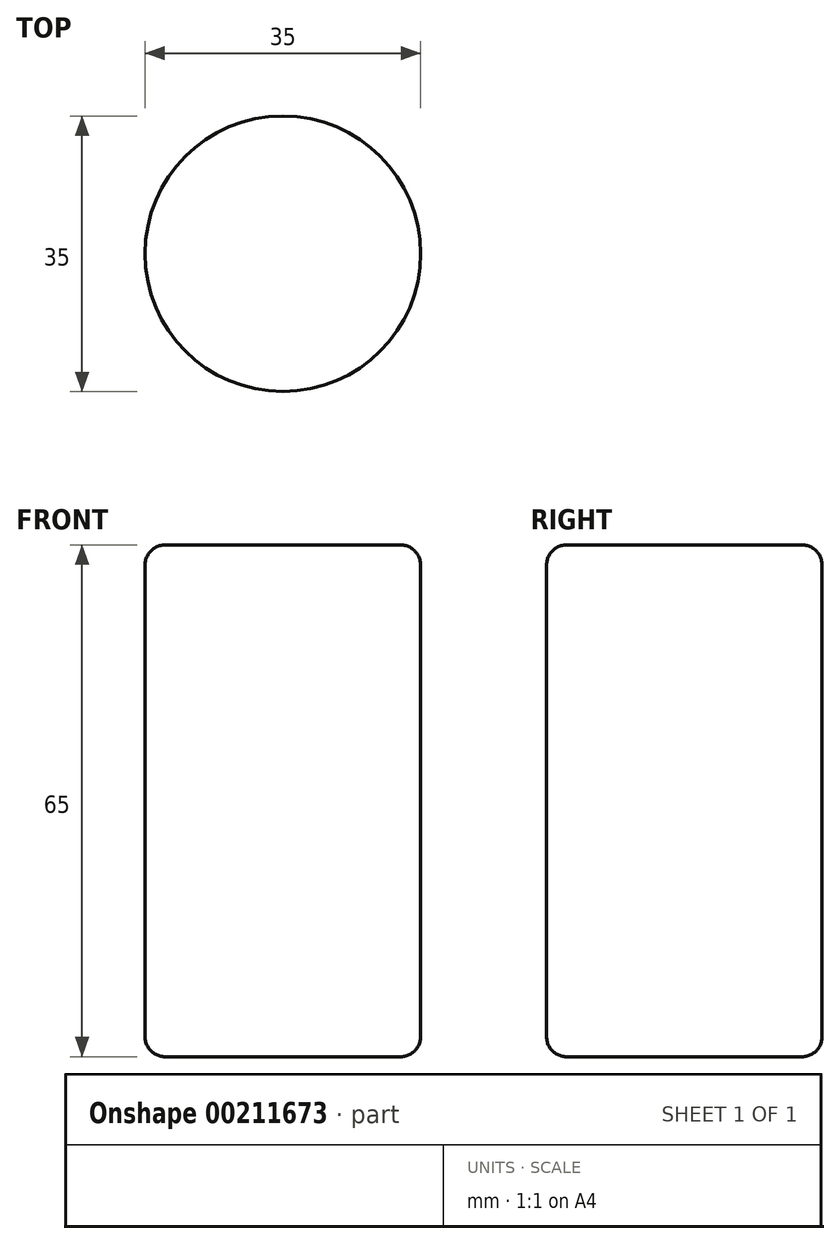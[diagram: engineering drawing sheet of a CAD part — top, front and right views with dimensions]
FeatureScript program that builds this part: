
annotation { "Feature Type Name" : "Feature", "Feature Type Description" : "" }
export const myFeature = defineFeature(function(context is Context, id is Id, definition is map)
    precondition{}
    {
        {
            var Q0;
            Q0=qCreatedBy(makeId("Front.planeOp"),FACE);
            var sketch = newSketch(context, id + "F0", { "sketchPlane" : qUnion([Q0])});
            skLineSegment(sketch, "E0.bottom", {"start": v(0, 0) * mm, "end": v(17.5, 0) * mm});
            skLineSegment(sketch, "E0.top", {"start": v(0, 65) * mm, "end": v(17.5, 65) * mm});
            skLineSegment(sketch, "E0.left", {"start": v(0, 0) * mm, "end": v(0, 65) * mm});
            skLineSegment(sketch, "E0.right", {"start": v(17.5, 0) * mm, "end": v(17.5, 65) * mm});
            skSolve(sketch);
        }
        {
            var Q0;
            Q0=makeQuery(id+"F0.imprint","IMPRINT",FACE,{"disambiguationData":[TD([[makeQuery(id+"F0.imprint","IMPRINT",EDGE,{"derivedFrom":sQuery(id+"F0.wireOp",EDGE,"E0.bottom")}),1.0]])]});
            var Q1;
            Q1=sQuery(id+"F0.wireOp",EDGE,"E0.left");
            revolve(context, id + "F1", {"entities" : qUnion([Q0]), "axis" : qUnion([Q1]), "revolveType" : RevolveType.FULL});
        }
        {
            var Q0;
            Q0=makeQuery(id+"F1.opRevolve","SWEPT_EDGE",EDGE,{"disambiguationData":[OSD([sQuery(id+"F0.wireOp",EDGE,"E0.top"),sQuery(id+"F0.wireOp",EDGE,"E0.right")])]});
            var Q1;
            Q1=makeQuery(id+"F1.opRevolve","SWEPT_EDGE",EDGE,{"disambiguationData":[OSD([sQuery(id+"F0.wireOp",EDGE,"E0.bottom"),sQuery(id+"F0.wireOp",EDGE,"E0.right")])]});
            fillet(context, id + "F2", {"entities" : qUnion([Q0, Q1]), "radius" : 2.54 * mm, "tangentPropagation" : true, "allowEdgeOverflow" : false});
        }
    });
